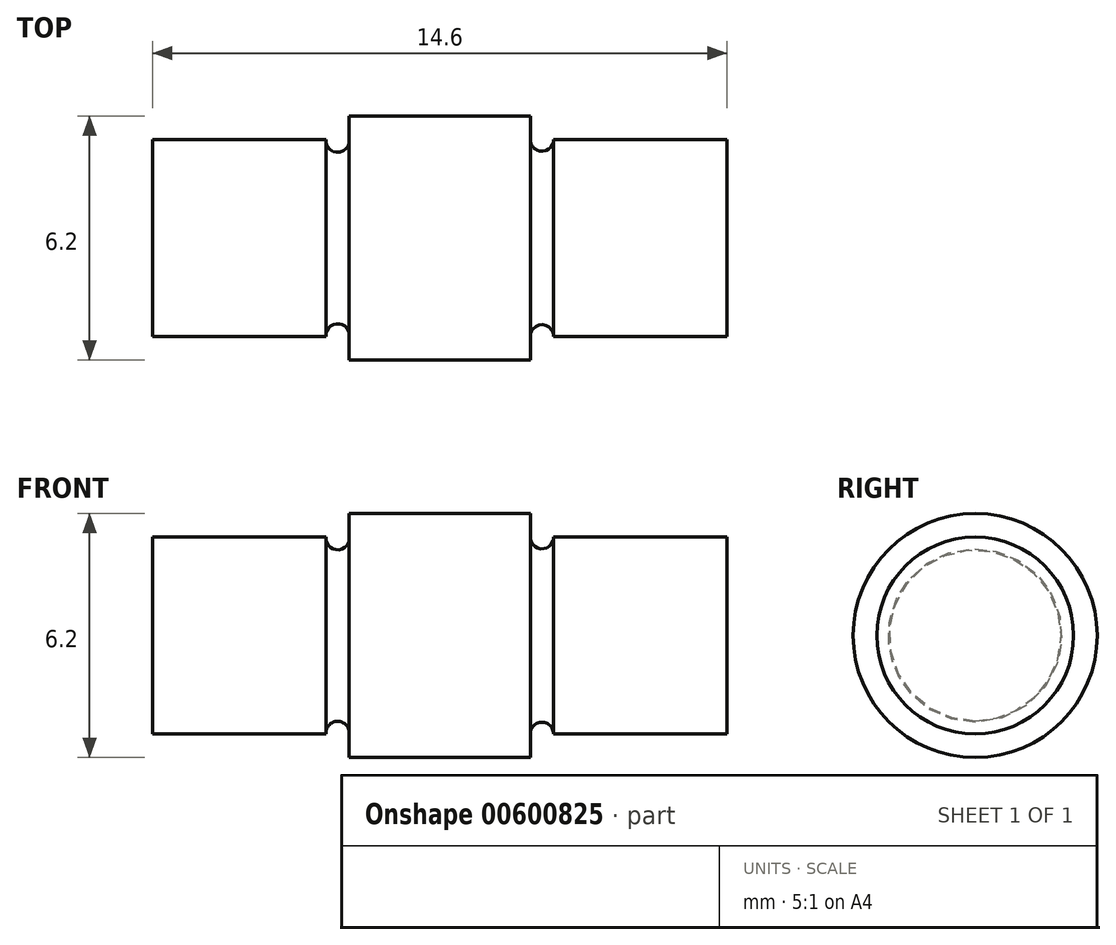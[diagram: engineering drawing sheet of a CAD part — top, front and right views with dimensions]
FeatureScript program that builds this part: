
annotation { "Feature Type Name" : "Feature", "Feature Type Description" : "" }
export const myFeature = defineFeature(function(context is Context, id is Id, definition is map)
    precondition{}
    {
        {
            var Q0;
            Q0=qCreatedBy(makeId("Front.planeOp"),FACE);
            var sketch = newSketch(context, id + "F0", { "sketchPlane" : qUnion([Q0])});
            skLineSegment(sketch, "E0", {"start": v(-17.93, 2.5) * mm, "end": v(-13.52, 2.5) * mm});
            skLineSegment(sketch, "E1", {"start": v(-17.93, 0) * mm, "end": v(-17.93, 2.5) * mm});
            skArc(sketch, "E2", {"start": v(-13.52, 2.5) * mm, "mid": v(-13.23, 2.18) * mm, "end": v(-12.93, 2.5) * mm});
            skLineSegment(sketch, "E3", {"start": v(-12.93, 2.5) * mm, "end": v(-12.93, 3.1) * mm});
            skLineSegment(sketch, "E4", {"start": v(-12.93, 3.1) * mm, "end": v(-8.33, 3.1) * mm});
            skLineSegment(sketch, "E5", {"start": v(-8.33, 3.1) * mm, "end": v(-8.33, 2.5) * mm});
            skArc(sketch, "E6", {"start": v(-8.33, 2.5) * mm, "mid": v(-8.04, 2.2) * mm, "end": v(-7.74, 2.5) * mm});
            skLineSegment(sketch, "E7", {"start": v(-7.74, 2.5) * mm, "end": v(-3.33, 2.5) * mm});
            skLineSegment(sketch, "E8", {"start": v(-3.33, 2.5) * mm, "end": v(-3.33, 0) * mm});
            skLineSegment(sketch, "E9", {"start": v(-3.33, 0) * mm, "end": v(-17.93, 0) * mm});
            skSolve(sketch);
        }
        {
            var Q0;
            Q0=makeQuery(id+"F0.imprint","IMPRINT",FACE,{"disambiguationData":[TD([[makeQuery(id+"F0.imprint","IMPRINT",EDGE,{"derivedFrom":sQuery(id+"F0.wireOp",EDGE,"E0")}),-1.0]])]});
            var Q1;
            Q1=sQuery(id+"F0.wireOp",EDGE,"E9");
            revolve(context, id + "F1", {"entities" : qUnion([Q0]), "axis" : qUnion([Q1]), "revolveType" : RevolveType.FULL});
        }
    });
